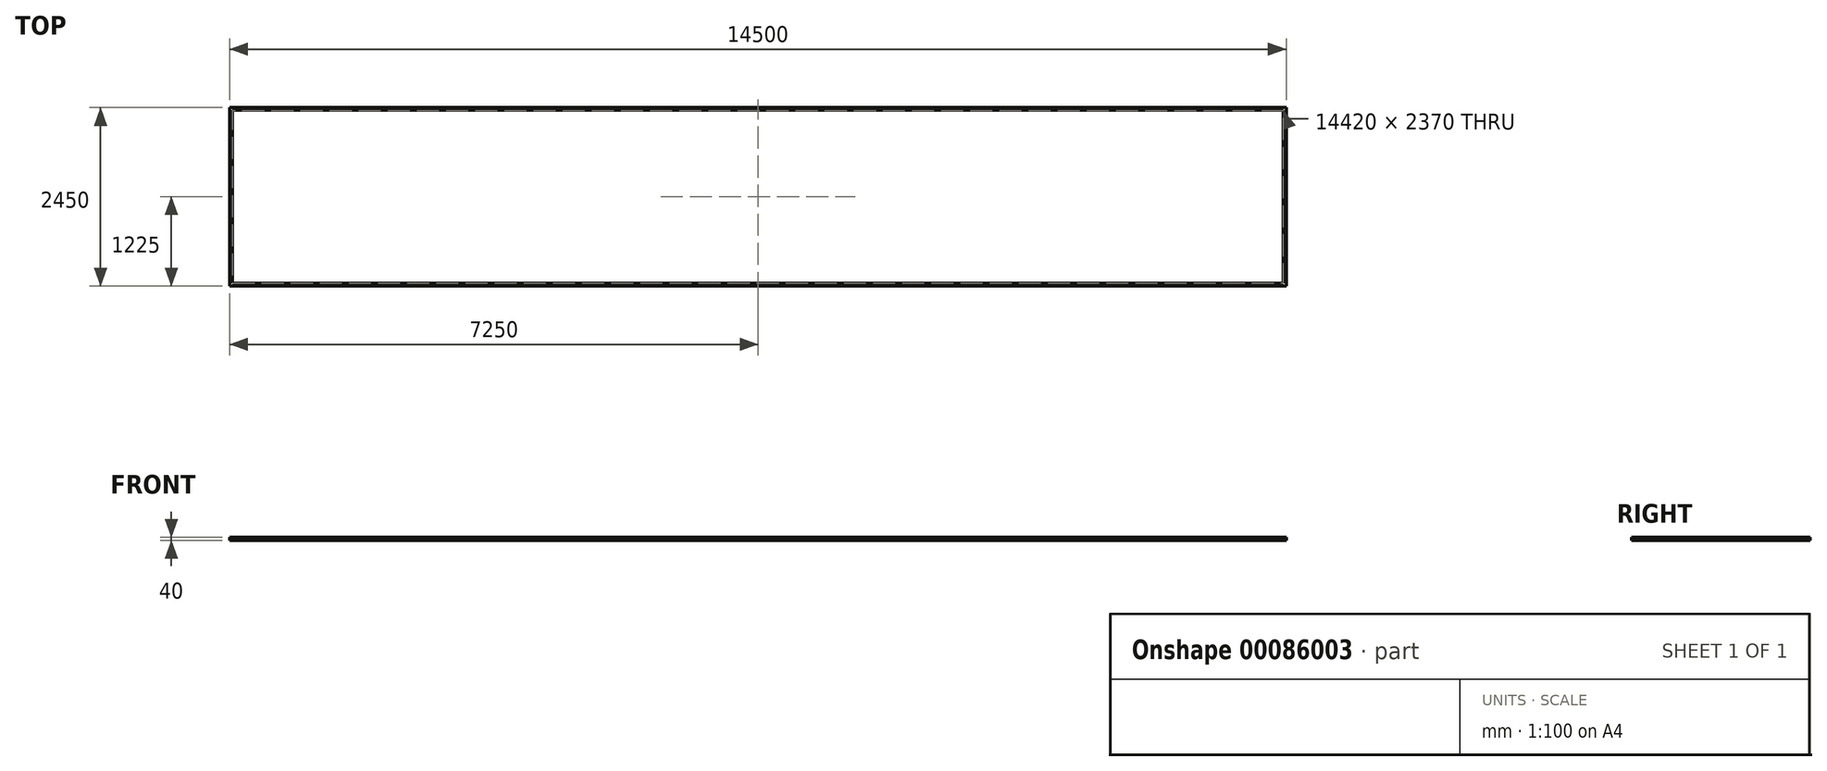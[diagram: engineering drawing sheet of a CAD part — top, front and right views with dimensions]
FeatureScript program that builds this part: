
annotation { "Feature Type Name" : "Feature", "Feature Type Description" : "" }
export const myFeature = defineFeature(function(context is Context, id is Id, definition is map)
    precondition{}
    {
        {
            var Q0;
            Q0=qCreatedBy(makeId("Top.planeOp"),FACE);
            var sketch = newSketch(context, id + "F0", { "sketchPlane" : qUnion([Q0])});
            skLineSegment(sketch, "E0.bottom", {"start": v(7250, 1225) * mm, "end": v(-7250, 1225) * mm});
            skLineSegment(sketch, "E0.top", {"start": v(7250, -1225) * mm, "end": v(-7250, -1225) * mm});
            skLineSegment(sketch, "E0.left", {"start": v(7250, 1225) * mm, "end": v(7250, -1225) * mm});
            skLineSegment(sketch, "E0.right", {"start": v(-7250, 1225) * mm, "end": v(-7250, -1225) * mm});
            skPoint(sketch, "E0.middle", {"position": v(0, 0) * mm});
            skLineSegment(sketch, "E1.bottom", {"start": v(7210, 1185) * mm, "end": v(-7210, 1185) * mm});
            skLineSegment(sketch, "E1.top", {"start": v(7210, -1185) * mm, "end": v(-7210, -1185) * mm});
            skLineSegment(sketch, "E1.left", {"start": v(7210, 1185) * mm, "end": v(7210, -1185) * mm});
            skLineSegment(sketch, "E1.right", {"start": v(-7210, 1185) * mm, "end": v(-7210, -1185) * mm});
            skLineSegment(sketch, "E2.bottom", {"start": v(-5450, 1185) * mm, "end": v(-5410, 1185) * mm});
            skLineSegment(sketch, "E2.top", {"start": v(-5450, -1185) * mm, "end": v(-5410, -1185) * mm});
            skLineSegment(sketch, "E2.left", {"start": v(-5450, 1185) * mm, "end": v(-5450, -1185) * mm});
            skLineSegment(sketch, "E2.right", {"start": v(-5410, 1185) * mm, "end": v(-5410, -1185) * mm});
            skLineSegment(sketch, "E3.bottom", {"start": v(-3650, 1185) * mm, "end": v(-3610, 1185) * mm});
            skLineSegment(sketch, "E3.top", {"start": v(-3650, -1185) * mm, "end": v(-3610, -1185) * mm});
            skLineSegment(sketch, "E3.left", {"start": v(-3650, 1185) * mm, "end": v(-3650, -1185) * mm});
            skLineSegment(sketch, "E3.right", {"start": v(-3610, 1185) * mm, "end": v(-3610, -1185) * mm});
            skLineSegment(sketch, "E4.bottom", {"start": v(-1850, 1185) * mm, "end": v(-1810, 1185) * mm});
            skLineSegment(sketch, "E4.top", {"start": v(-1850, -1185) * mm, "end": v(-1810, -1185) * mm});
            skLineSegment(sketch, "E4.left", {"start": v(-1810, 1185) * mm, "end": v(-1810, -1185) * mm});
            skLineSegment(sketch, "E4.right", {"start": v(-1850, 1185) * mm, "end": v(-1850, -1185) * mm});
            skLineSegment(sketch, "E5.bottom", {"start": v(1750, 1185) * mm, "end": v(1790, 1185) * mm});
            skLineSegment(sketch, "E5.top", {"start": v(1750, -1185) * mm, "end": v(1790, -1185) * mm});
            skLineSegment(sketch, "E5.left", {"start": v(1750, 1185) * mm, "end": v(1750, -1185) * mm});
            skLineSegment(sketch, "E5.right", {"start": v(1790, 1185) * mm, "end": v(1790, -1185) * mm});
            skLineSegment(sketch, "E6.bottom", {"start": v(3550, 1185) * mm, "end": v(3590, 1185) * mm});
            skLineSegment(sketch, "E6.top", {"start": v(3550, -1185) * mm, "end": v(3590, -1185) * mm});
            skLineSegment(sketch, "E6.left", {"start": v(3550, 1185) * mm, "end": v(3550, -1185) * mm});
            skLineSegment(sketch, "E6.right", {"start": v(3590, 1185) * mm, "end": v(3590, -1185) * mm});
            skLineSegment(sketch, "E7.bottom", {"start": v(-50, 1185) * mm, "end": v(-10, 1185) * mm});
            skLineSegment(sketch, "E7.top", {"start": v(-50, -1185) * mm, "end": v(-10, -1185) * mm});
            skLineSegment(sketch, "E7.left", {"start": v(-50, 1185) * mm, "end": v(-50, -1185) * mm});
            skLineSegment(sketch, "E7.right", {"start": v(-10, 1185) * mm, "end": v(-10, -1185) * mm});
            skLineSegment(sketch, "E8.bottom", {"start": v(5350, 1185) * mm, "end": v(5390, 1185) * mm});
            skLineSegment(sketch, "E8.top", {"start": v(5350, -1185) * mm, "end": v(5390, -1185) * mm});
            skLineSegment(sketch, "E8.left", {"start": v(5350, 1185) * mm, "end": v(5350, -1185) * mm});
            skLineSegment(sketch, "E8.right", {"start": v(5390, 1185) * mm, "end": v(5390, -1185) * mm});
            skSolve(sketch);
        }
        {
            var Q0;
            Q0=makeQuery(id+"F0.imprint","IMPRINT",FACE,{"disambiguationData":[TD([[makeQuery(id+"F0.imprint","IMPRINT",EDGE,{"derivedFrom":sQuery(id+"F0.wireOp",EDGE,"E2.bottom")}),-1.0]])]});
            var Q1;
            Q1=makeQuery(id+"F0.imprint","IMPRINT",FACE,{"disambiguationData":[TD([[makeQuery(id+"F0.imprint","IMPRINT",EDGE,{"derivedFrom":sQuery(id+"F0.wireOp",EDGE,"E3.bottom")}),-1.0]])]});
            var Q2;
            Q2=makeQuery(id+"F0.imprint","IMPRINT",FACE,{"disambiguationData":[TD([[makeQuery(id+"F0.imprint","IMPRINT",EDGE,{"derivedFrom":sQuery(id+"F0.wireOp",EDGE,"E0.bottom")}),1.0]])]});
            var Q3;
            Q3=makeQuery(id+"F0.imprint","IMPRINT",FACE,{"disambiguationData":[TD([[makeQuery(id+"F0.imprint","IMPRINT",EDGE,{"derivedFrom":sQuery(id+"F0.wireOp",EDGE,"E4.bottom")}),-1.0]])]});
            var Q4;
            Q4=makeQuery(id+"F0.imprint","IMPRINT",FACE,{"disambiguationData":[TD([[makeQuery(id+"F0.imprint","IMPRINT",EDGE,{"derivedFrom":sQuery(id+"F0.wireOp",EDGE,"E7.bottom")}),-1.0]])]});
            var Q5;
            Q5=makeQuery(id+"F0.imprint","IMPRINT",FACE,{"disambiguationData":[TD([[makeQuery(id+"F0.imprint","IMPRINT",EDGE,{"derivedFrom":sQuery(id+"F0.wireOp",EDGE,"E5.bottom")}),-1.0]])]});
            var Q6;
            Q6=makeQuery(id+"F0.imprint","IMPRINT",FACE,{"disambiguationData":[TD([[makeQuery(id+"F0.imprint","IMPRINT",EDGE,{"derivedFrom":sQuery(id+"F0.wireOp",EDGE,"E6.bottom")}),-1.0]])]});
            var Q7;
            Q7=makeQuery(id+"F0.imprint","IMPRINT",FACE,{"disambiguationData":[TD([[makeQuery(id+"F0.imprint","IMPRINT",EDGE,{"derivedFrom":sQuery(id+"F0.wireOp",EDGE,"E8.bottom")}),-1.0]])]});
            extrude(context, id + "F1", {"entities" : qUnion([Q0, Q1, Q2, Q3, Q4, Q5, Q6, Q7]), "oppositeDirection" : true, "depth" : 40 * mm});
        }
    });
